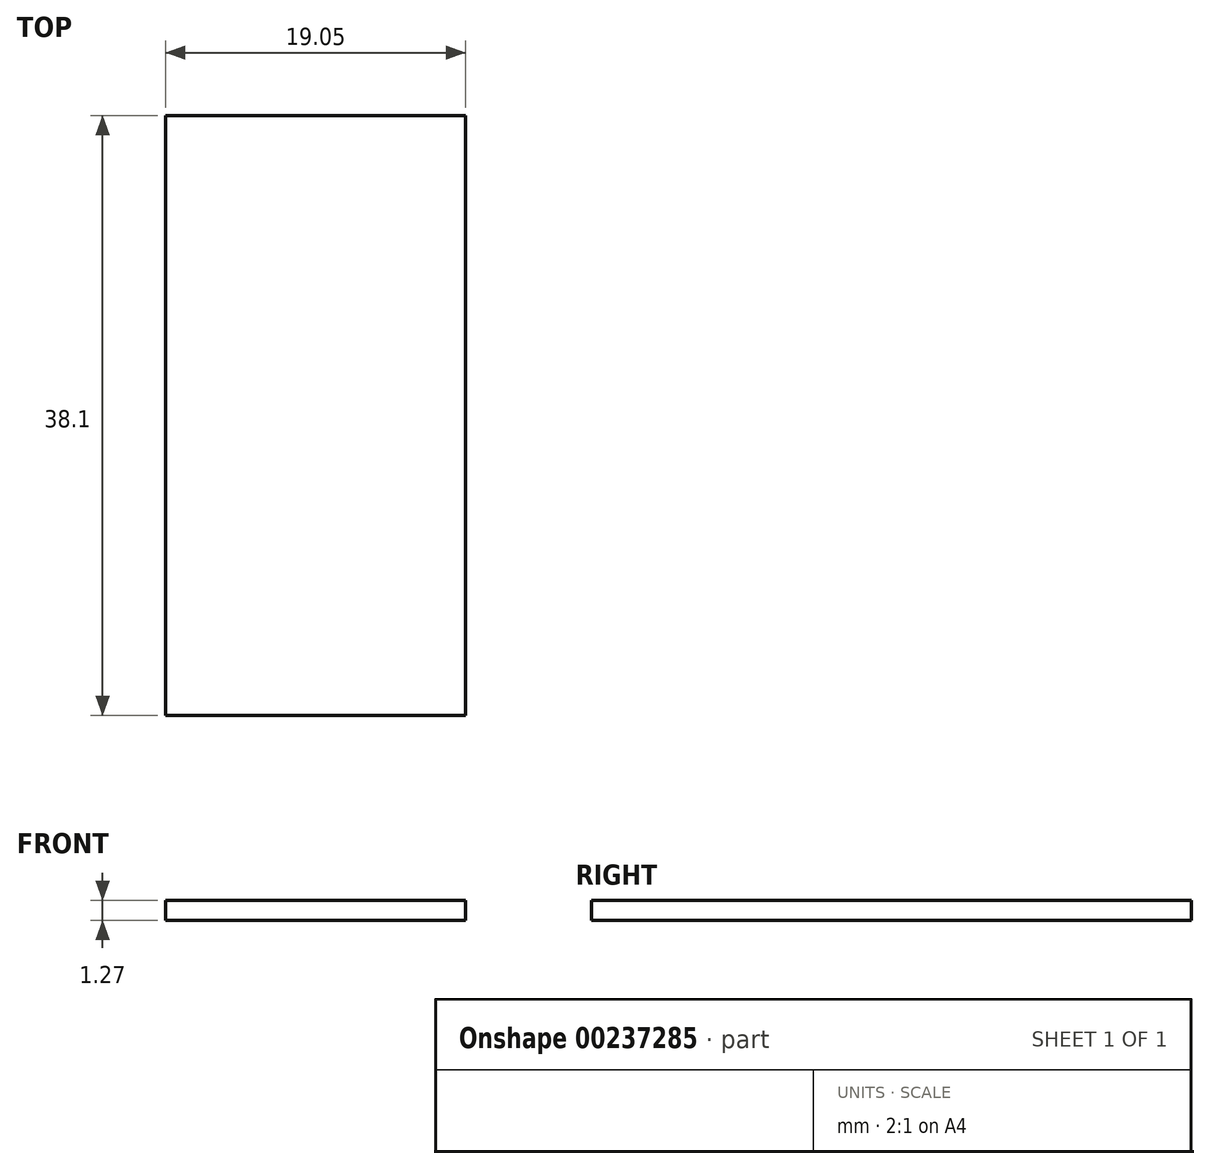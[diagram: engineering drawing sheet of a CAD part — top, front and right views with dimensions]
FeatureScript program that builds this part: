
annotation { "Feature Type Name" : "Feature", "Feature Type Description" : "" }
export const myFeature = defineFeature(function(context is Context, id is Id, definition is map)
    precondition{}
    {
        {
            var Q0;
            Q0=qCreatedBy(makeId("Top.planeOp"),FACE);
            var sketch = newSketch(context, id + "F0", { "sketchPlane" : qUnion([Q0])});
            skLineSegment(sketch, "E0.bottom", {"start": v(0, 0) * mm, "end": v(19.05, 0) * mm});
            skLineSegment(sketch, "E0.top", {"start": v(0, -38.1) * mm, "end": v(19.05, -38.1) * mm});
            skLineSegment(sketch, "E0.left", {"start": v(0, 0) * mm, "end": v(0, -38.1) * mm});
            skLineSegment(sketch, "E0.right", {"start": v(19.05, 0) * mm, "end": v(19.05, -38.1) * mm});
            skSolve(sketch);
        }
        {
            var Q0;
            Q0=makeQuery(id+"F0.imprint","IMPRINT",FACE,{"disambiguationData":[TD([[makeQuery(id+"F0.imprint","IMPRINT",EDGE,{"derivedFrom":sQuery(id+"F0.wireOp",EDGE,"E0.bottom")}),-1.0]])]});
            extrude(context, id + "F1", {"entities" : qUnion([Q0]), "depth" : 1.27 * mm});
        }
    });
